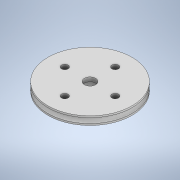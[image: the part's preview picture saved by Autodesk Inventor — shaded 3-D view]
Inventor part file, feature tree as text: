
AUTODESK INVENTOR PART (.ipt)
format: ipt  version: 2021 (Build 250183000, 183)  size: 342,528 bytes
history: native  units: mm
features: sketch x4, extrude x3, other x2, revolve x1, direct_edit x1, move_body x1
ambient origin geometry x8: Origin, YZ Plane, XZ Plane, XY Plane, X Axis, Y Axis, Z Axis, Center Point
bodies: Volumenkörper1 (feature_tree), Volumenkörper2 (feature_tree)
feature tree (12):
  other  "Servo_Rad_20_Durchmesser"
  extrude  "Extrusion1"  Depth=2.0mm TaperAngle=0.0deg
  revolve  "Umdrehung1"
  other  "Kombinieren1"
  extrude  "Extrusion2"  TaperAngle=90.0deg  [1 undecoded]
  direct_edit  "Direktbearbeitung1"
  extrude  "Extrusion3"  Depth=7.0mm
  sketch  "Skizze1"  dims[d0=20.0mm d1=2.0mm d2=0.0mm]
  sketch  "Skizze2"  dims[d3=1.2mm d4=90.0deg]
  sketch  "Skizze3"  dims[d5=2.7mm d6=7.0mm]
  sketch  "Skizze4"  dims[d7=4.6mm d8=1.5mm d9=0.0mm d10=0.0mm d11=0.0mm d12=-1.0mm d13=1.6mm d14=0.0mm d15=6.0mm d16=40.0mm d18=360.0deg d20=4.95mm d21=0.0mm d22=0.5mm d23=0.872665mm d24=0.5mm d25=0.872665mm]
  move_body  "Verschieben1"
note: 1 required parameter value undecoded (feature->parameter linkage not recoverable at this tier; creation-order binding heuristic only, values carry confidence <= 0.55)
